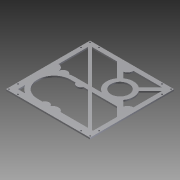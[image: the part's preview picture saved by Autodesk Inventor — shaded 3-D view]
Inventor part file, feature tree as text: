
AUTODESK INVENTOR PART (.ipt)
format: ipt  version: 2012 (Build 160160000, 160)  size: 297,984 bytes
history: native  units: in
note: dims shown in document units (in); Inventor stores cm internally (conversion verified against a paired STEP export)
features: extrude x6, hole x4, fillet x4, chamfer x2, sketch x1
ambient origin geometry x8: Origin, YZ Plane, XZ Plane, XY Plane, X Axis, Y Axis, Z Axis, Center Point
feature tree (17):
  sketch  "Sketch1"  dims[d0=4.5in d1=7.0in d2=7.0in d3=4.5in d4=1.5in d5=2.25in d6=2.25in d10=0.125in d11=0.125in d12=0.125in d15=0.125in d16=0.875in d17=0.875in d18=0.125in d19=0.125in d20=0.875in d23=0.125in d24=0.125in d25=0.875in d26=0.125in d27=0.125in d28=0.125in d29=0.125in d30=0.875in d34=0.125in d35=0.125in d36=0.125in d37=0.125in d38=0.875in d39=0.125in d40=0.125in d41=0.125in d42=0.125in d43=0.125in d44=0.125in d45=0.125in d46=0.875in d47=0.125in d48=0.125in d49=0.125in d50=0.125in d51=0.875in d52=0.125in d55=2.75in d56=2.0in d57=2.0in d93=2.75in d94=0.625in d97=1.5in d98=1.5in d99=1.5in d100=1.5in d101=0.75in d102=0.75in d103=0.75in d104=0.75in d212=0.375in d216=0.1875in d218=45.0deg d222=0.2652in d226=1.125in d227=0.1875in d228=0.1875in d232=0.375in d234=1.125in d257=0.125in d258=0.0in d260=0.5in d261=0.5in d280=1.75in d281=1.75in d285=0.125in d286=0.0in d287=0.375in d288=0.2in d289=0.75in d290=0.375in d291=0.25in d292=0.5635in d293=1.0in d294=0.8108in d296=0.35in d298=1.0in d299=0.0in d300=0.125in d301=0.1875in d302=1.125in d303=0.125in d304=0.1875in d305=0.1875in d307=0.375in d308=1.0in d309=0.0in d310=0.125in d311=1.75in d312=1.0in d313=0.125in d314=0.75in d315=0.375in d316=0.25in d317=0.5635in d318=1.0in d319=0.8108in d320=1.875in d321=1.0in d322=0.125in d323=0.75in d324=0.375in d325=0.25in d326=0.5635in d327=1.0in d328=0.8108in d329=0.5in d330=3.5in d331=3.5in d332=0.5in d336=0.5in d337=3.5in d338=0.35in d339=0.25in d340=0.75in d341=0.375in d342=0.25in d343=0.5635in d344=1.0in d345=0.8108in d347=0.375in d348=0.0625in d349=0.125in d350=45.0deg d351=0.0625in d352=0.125in d353=45.0deg d354=0.375in d356=0.375in d363=1.0in d364=0.0in d365=0.125in d369=0.375in d370=3.5in d371=0.5in d372=0.125in d373=0.125in d374=0.375in d375=0.1875in d376=0.125in d377=0.125in d378=0.125in d379=0.0in]
  extrude  "Extrusion12"  Depth=7.0in
  extrude  "Extrusion13"  Depth=7.0in
  hole  "Hole9"  [1 undecoded]
  extrude  "Extrusion14"  Depth=1.5in
  fillet  "Fillet2"  Radius=2.25in
  fillet  "Fillet3"  Radius=2.25in
  extrude  "Extrusion15"  Depth=0.125in
  fillet  "Fillet4"  Radius=0.125in
  hole  "Hole10"  [1 undecoded]
  hole  "Hole11"  [1 undecoded]
  hole  "Hole12"  [1 undecoded]
  chamfer  "Chamfer1"  Distance=0.875in
  chamfer  "Chamfer2"  Distance=0.125in
  extrude  "Extrusion16"  Depth=0.125in
  fillet  "Fillet6"  Radius=0.875in
  extrude  "Extrusion17"  Depth=0.125in
note: 4 required parameter values undecoded (feature->parameter linkage not recoverable at this tier; creation-order binding heuristic only, values carry confidence <= 0.55)
